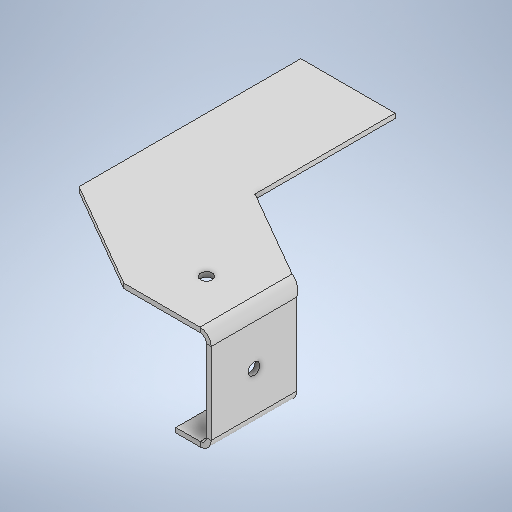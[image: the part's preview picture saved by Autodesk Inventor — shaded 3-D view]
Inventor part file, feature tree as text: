
AUTODESK INVENTOR PART (.ipt)
format: ipt  version: 2025 (Build 290162010, 162A)  size: 327,680 bytes
history: native  units: mm
features: sheet_metal_op x7, sketch x4, other x4, extrude x1, projected_geometry x1
ambient origin geometry x8: Origin, YZ Plane, XZ Plane, XY Plane, X Axis, Y Axis, Z Axis, Center Point
bodies: Solid1 (feature_tree)
feature tree (17):
  sheet_metal_op  "Face1"
  sheet_metal_op  "Flange1"
  sheet_metal_op  "Flange2"
  extrude  "Extrusion1"  Depth=120.0mm
  sketch  "Sketch1"  dims[d0=82.0mm d1=120.0mm]
  other  "Plate1"
  sketch  "Sketch4"  dims[d2=2.0mm]
  other  "Plate2"
  sheet_metal_op  "Bend1"
  sheet_metal_op  "Corner1"
  sketch  "Sketch5"  dims[d6=30.0deg]
  other  "Plate3"
  sheet_metal_op  "Bend2"
  sheet_metal_op  "Corner2"
  sketch  "Sketch6"  dims[d9=2.0mm d10=1.0mm d11=4.0mm d12=2.75mm d13=44.0mm d14=90.0deg d15=2.75mm d16=8.0mm d17=2.0mm d18=2.75mm d19=2.0mm d20=1.0mm d21=4.0mm d22=2.75mm d23=15.0mm d24=90.0deg d25=2.75mm d26=8.0mm d27=2.0mm d28=2.75mm d29=40.0mm d30=50.0mm d31=5.0mm d32=0.0mm d33=0.0mm d34=5.0mm d35=20.0mm d36=20.0mm]
  projected_geometry  "Projected Loop1"
  other  "Definition1"
